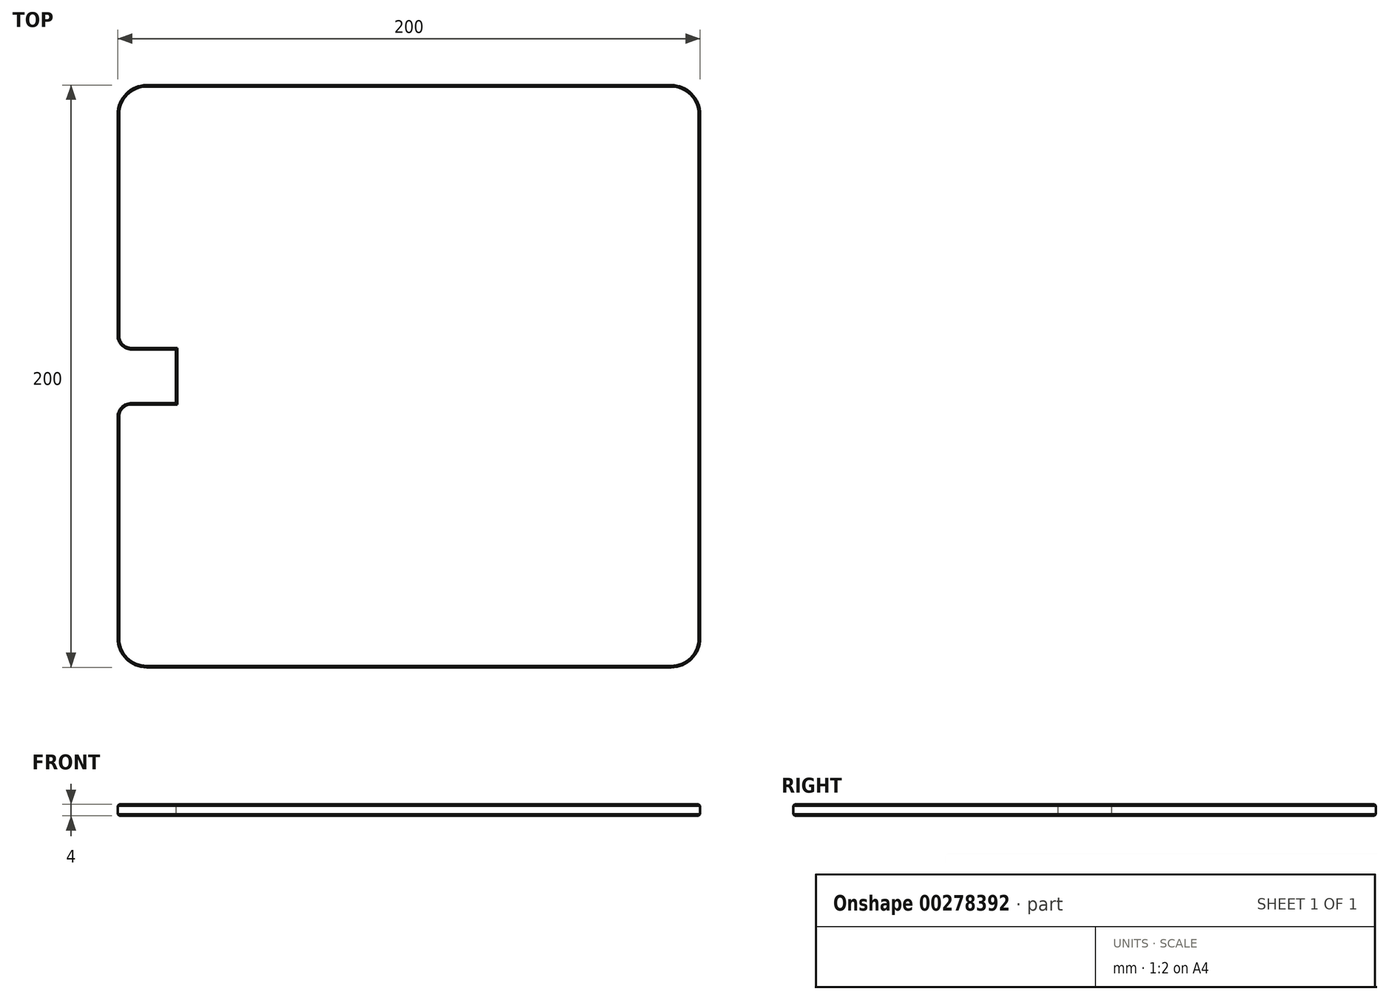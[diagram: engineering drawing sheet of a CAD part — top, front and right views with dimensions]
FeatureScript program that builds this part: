
annotation { "Feature Type Name" : "Feature", "Feature Type Description" : "" }
export const myFeature = defineFeature(function(context is Context, id is Id, definition is map)
    precondition{}
    {
        {
            var Q0;
            Q0=qCreatedBy(makeId("Top.planeOp"),FACE);
            var sketch = newSketch(context, id + "F0", { "sketchPlane" : qUnion([Q0])});
            skLineSegment(sketch, "E0.bottom", {"start": v(90, -100) * mm, "end": v(-90, -100) * mm});
            skLineSegment(sketch, "E0.top", {"start": v(90, 100) * mm, "end": v(-90, 100) * mm});
            skLineSegment(sketch, "E0.left", {"start": v(100, -90) * mm, "end": v(100, 90) * mm});
            skLineSegment(sketch, "E0.right", {"start": v(-100, -90) * mm, "end": v(-100, -14) * mm});
            skPoint(sketch, "E0.middle", {"position": v(0, 0) * mm});
            skLineSegment(sketch, "E1", {"start": v(-95.2, 9.2) * mm, "end": v(-80, 9.2) * mm});
            skLineSegment(sketch, "E2", {"start": v(-80, 9.2) * mm, "end": v(-80, -9.2) * mm});
            skLineSegment(sketch, "E3", {"start": v(-80, -9.2) * mm, "end": v(-95.2, -9.2) * mm});
            skLineSegment(sketch, "E4.trimOffspring", {"start": v(-100, 14) * mm, "end": v(-100, 90) * mm});
            skLineSegment(sketch, "E5", {"start": v(-80, 0) * mm, "end": v(0, 0) * mm, "construction": true});
            skPoint(sketch, "E6.visualSharp", {"position": v(-100, 9.2) * mm});
            skArc(sketch, "E6.filletArc", {"start": v(-100, 14) * mm, "mid": v(-98.6, 10.6) * mm, "end": v(-95.2, 9.2) * mm});
            skPoint(sketch, "E7.visualSharp", {"position": v(-100, -9.2) * mm});
            skArc(sketch, "E7.filletArc", {"start": v(-95.2, -9.2) * mm, "mid": v(-98.6, -10.6) * mm, "end": v(-100, -14) * mm});
            skPoint(sketch, "E8.visualSharp", {"position": v(-100, 100) * mm});
            skArc(sketch, "E8.filletArc", {"start": v(-90, 100) * mm, "mid": v(-97.07, 97.07) * mm, "end": v(-100, 90) * mm});
            skPoint(sketch, "E9.visualSharp", {"position": v(100, 100) * mm});
            skArc(sketch, "E9.filletArc", {"start": v(100, 90) * mm, "mid": v(97.07, 97.07) * mm, "end": v(90, 100) * mm});
            skPoint(sketch, "E10.visualSharp", {"position": v(100, -100) * mm});
            skArc(sketch, "E10.filletArc", {"start": v(90, -100) * mm, "mid": v(97.07, -97.07) * mm, "end": v(100, -90) * mm});
            skPoint(sketch, "E11.visualSharp", {"position": v(-100, -100) * mm});
            skArc(sketch, "E11.filletArc", {"start": v(-100, -90) * mm, "mid": v(-97.07, -97.07) * mm, "end": v(-90, -100) * mm});
            skLineSegment(sketch, "E12", {"start": v(0, 0) * mm, "end": v(0, 100) * mm, "construction": true});
            skLineSegment(sketch, "E13", {"start": v(0, 0) * mm, "end": v(100, 0) * mm, "construction": true});
            skSolve(sketch);
        }
        {
            var Q0;
            Q0 = qSketchRegion(id + "F0", true);
            extrude(context, id + "F1", {"entities" : qUnion([Q0]), "depth" : 4 * mm, "offsetDistance" : 25 * mm});
        }
        {
            var Q0;
            Q0=makeQuery(id+"F1.opExtrude","CAP_FACE",FACE,{"disambiguationData":[OSD([sQuery(id+"F0.wireOp",EDGE,"E0.bottom"),sQuery(id+"F0.wireOp",EDGE,"E0.top"),sQuery(id+"F0.wireOp",EDGE,"E0.left"),sQuery(id+"F0.wireOp",EDGE,"E0.right"),sQuery(id+"F0.wireOp",EDGE,"E1"),sQuery(id+"F0.wireOp",EDGE,"E2"),sQuery(id+"F0.wireOp",EDGE,"E3"),sQuery(id+"F0.wireOp",EDGE,"E4.trimOffspring"),sQuery(id+"F0.wireOp",EDGE,"E6.filletArc"),sQuery(id+"F0.wireOp",EDGE,"E7.filletArc"),sQuery(id+"F0.wireOp",EDGE,"E8.filletArc"),sQuery(id+"F0.wireOp",EDGE,"E9.filletArc"),sQuery(id+"F0.wireOp",EDGE,"E10.filletArc"),sQuery(id+"F0.wireOp",EDGE,"E11.filletArc")])],"isStart":false});
            var Q1;
            Q1=makeQuery(id+"F1.opExtrude","CAP_FACE",FACE,{"disambiguationData":[OSD([sQuery(id+"F0.wireOp",EDGE,"E0.bottom"),sQuery(id+"F0.wireOp",EDGE,"E0.top"),sQuery(id+"F0.wireOp",EDGE,"E0.left"),sQuery(id+"F0.wireOp",EDGE,"E0.right"),sQuery(id+"F0.wireOp",EDGE,"E1"),sQuery(id+"F0.wireOp",EDGE,"E2"),sQuery(id+"F0.wireOp",EDGE,"E3"),sQuery(id+"F0.wireOp",EDGE,"E4.trimOffspring"),sQuery(id+"F0.wireOp",EDGE,"E6.filletArc"),sQuery(id+"F0.wireOp",EDGE,"E7.filletArc"),sQuery(id+"F0.wireOp",EDGE,"E8.filletArc"),sQuery(id+"F0.wireOp",EDGE,"E9.filletArc"),sQuery(id+"F0.wireOp",EDGE,"E10.filletArc"),sQuery(id+"F0.wireOp",EDGE,"E11.filletArc")])],"isStart":true});
            chamfer(context, id + "F2", {"entities" : qUnion([Q0, Q1]), "width" : 0.5 * mm, "tangentPropagation" : true});
        }
    });
